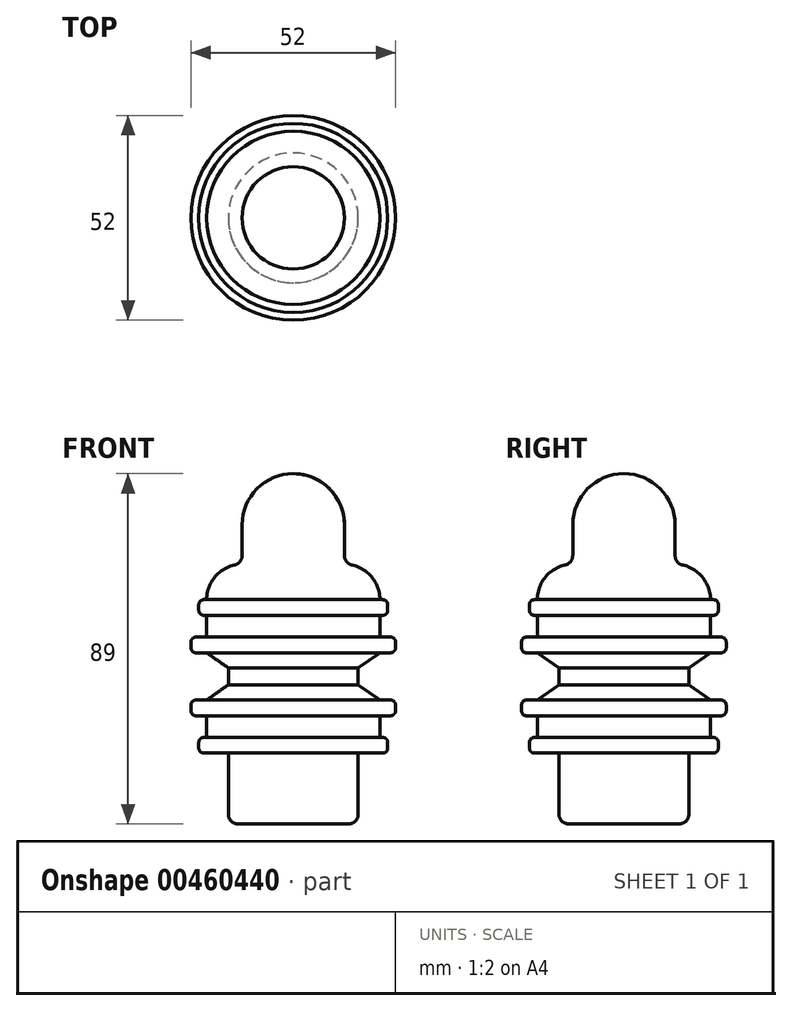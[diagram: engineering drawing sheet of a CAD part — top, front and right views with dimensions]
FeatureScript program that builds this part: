
annotation { "Feature Type Name" : "Feature", "Feature Type Description" : "" }
export const myFeature = defineFeature(function(context is Context, id is Id, definition is map)
    precondition{}
    {
        {
            var Q0;
            Q0=qCreatedBy(makeId("Front.planeOp"),FACE);
            var sketch = newSketch(context, id + "F0", { "sketchPlane" : qUnion([Q0])});
            skArc(sketch, "E0", {"start": v(13, -13) * mm, "mid": v(9.2, -3.8) * mm, "end": v(0, 0) * mm});
            skLineSegment(sketch, "E1", {"start": v(13, -13) * mm, "end": v(13, -23) * mm});
            skArc(sketch, "E2", {"start": v(22, -32) * mm, "mid": v(19.36, -25.64) * mm, "end": v(13, -23) * mm});
            skLineSegment(sketch, "E3", {"start": v(22, -32) * mm, "end": v(24, -32) * mm});
            skLineSegment(sketch, "E4", {"start": v(24, -36) * mm, "end": v(22, -36) * mm});
            skLineSegment(sketch, "E5", {"start": v(22, -36) * mm, "end": v(22, -41.5) * mm});
            skLineSegment(sketch, "E6", {"start": v(22, -41.5) * mm, "end": v(26, -41.5) * mm});
            skLineSegment(sketch, "E7", {"start": v(26, -41.5) * mm, "end": v(26, -45.5) * mm});
            skLineSegment(sketch, "E8", {"start": v(26, -45.5) * mm, "end": v(22, -45.5) * mm});
            skLineSegment(sketch, "E9", {"start": v(22, -45.5) * mm, "end": v(16.5, -49.35) * mm});
            skLineSegment(sketch, "E10", {"start": v(16.5, -49.35) * mm, "end": v(16.5, -53.65) * mm});
            skLineSegment(sketch, "E11", {"start": v(16.5, -53.65) * mm, "end": v(22, -57.5) * mm});
            skLineSegment(sketch, "E12", {"start": v(22, -57.5) * mm, "end": v(26, -57.5) * mm});
            skLineSegment(sketch, "E13", {"start": v(26, -57.5) * mm, "end": v(26, -61.5) * mm});
            skLineSegment(sketch, "E14", {"start": v(26, -61.5) * mm, "end": v(22, -61.5) * mm});
            skLineSegment(sketch, "E15", {"start": v(22, -61.5) * mm, "end": v(22, -67) * mm});
            skLineSegment(sketch, "E16", {"start": v(22, -67) * mm, "end": v(24, -67) * mm});
            skLineSegment(sketch, "E17", {"start": v(24, -71) * mm, "end": v(16.5, -71) * mm});
            skLineSegment(sketch, "E18", {"start": v(16.5, -71) * mm, "end": v(16.5, -89) * mm});
            skLineSegment(sketch, "E19", {"start": v(16.5, -89) * mm, "end": v(0, -89) * mm});
            skLineSegment(sketch, "E20", {"start": v(0, -89) * mm, "end": v(0, 0) * mm});
            skLineSegment(sketch, "E21", {"start": v(24, -67) * mm, "end": v(24, -71) * mm});
            skLineSegment(sketch, "E22", {"start": v(24, -36) * mm, "end": v(24, -32) * mm});
            skSolve(sketch);
        }
        {
            var Q0;
            Q0=makeQuery(id+"F0.imprint","IMPRINT",FACE,{"disambiguationData":[TD([[makeQuery(id+"F0.imprint","IMPRINT",EDGE,{"derivedFrom":sQuery(id+"F0.wireOp",EDGE,"E0")}),1.0]])]});
            var Q1;
            Q1=sQuery(id+"F0.wireOp",EDGE,"E20");
            revolve(context, id + "F1", {"entities" : qUnion([Q0]), "axis" : qUnion([Q1]), "revolveType" : RevolveType.FULL});
        }
        {
            var Q0;
            Q0=makeQuery(id+"F1.opRevolve","SWEPT_EDGE",EDGE,{"disambiguationData":[OSD([sQuery(id+"F0.wireOp",EDGE,"E13"),sQuery(id+"F0.wireOp",EDGE,"E14")])]});
            var Q1;
            Q1=makeQuery(id+"F1.opRevolve","SWEPT_EDGE",EDGE,{"disambiguationData":[OSD([sQuery(id+"F0.wireOp",EDGE,"E16"),sQuery(id+"F0.wireOp",EDGE,"E21")])]});
            var Q2;
            Q2=makeQuery(id+"F1.opRevolve","SWEPT_EDGE",EDGE,{"disambiguationData":[OSD([sQuery(id+"F0.wireOp",EDGE,"E12"),sQuery(id+"F0.wireOp",EDGE,"E13")])]});
            var Q3;
            Q3=makeQuery(id+"F1.opRevolve","SWEPT_EDGE",EDGE,{"disambiguationData":[OSD([sQuery(id+"F0.wireOp",EDGE,"E7"),sQuery(id+"F0.wireOp",EDGE,"E8")])]});
            var Q4;
            Q4=makeQuery(id+"F1.opRevolve","SWEPT_EDGE",EDGE,{"disambiguationData":[OSD([sQuery(id+"F0.wireOp",EDGE,"E6"),sQuery(id+"F0.wireOp",EDGE,"E7")])]});
            var Q5;
            Q5=makeQuery(id+"F1.opRevolve","SWEPT_EDGE",EDGE,{"disambiguationData":[OSD([sQuery(id+"F0.wireOp",EDGE,"E4"),sQuery(id+"F0.wireOp",EDGE,"E22")])]});
            var Q6;
            Q6=makeQuery(id+"F1.opRevolve","SWEPT_EDGE",EDGE,{"disambiguationData":[OSD([sQuery(id+"F0.wireOp",EDGE,"E3"),sQuery(id+"F0.wireOp",EDGE,"E22")])]});
            var Q7;
            Q7=makeQuery(id+"F1.opRevolve","SWEPT_EDGE",EDGE,{"disambiguationData":[OSD([sQuery(id+"F0.wireOp",EDGE,"E17"),sQuery(id+"F0.wireOp",EDGE,"E21")])]});
            fillet(context, id + "F2", {"entities" : qUnion([Q0, Q1, Q2, Q3, Q4, Q5, Q6, Q7]), "radius" : 1.3 * mm, "tangentPropagation" : true, "allowEdgeOverflow" : false});
        }
        {
            var Q0;
            Q0=makeQuery(id+"F1.opRevolve","SWEPT_EDGE",EDGE,{"disambiguationData":[OSD([sQuery(id+"F0.wireOp",EDGE,"E18"),sQuery(id+"F0.wireOp",EDGE,"E19")])]});
            var Q1;
            Q1=makeQuery(id+"F1.opRevolve","SWEPT_EDGE",EDGE,{"disambiguationData":[OSD([sQuery(id+"F0.wireOp",EDGE,"E1"),sQuery(id+"F0.wireOp",EDGE,"E2")])]});
            fillet(context, id + "F3", {"entities" : qUnion([Q0, Q1]), "radius" : 2.5 * mm, "tangentPropagation" : true, "allowEdgeOverflow" : false});
        }
    });
